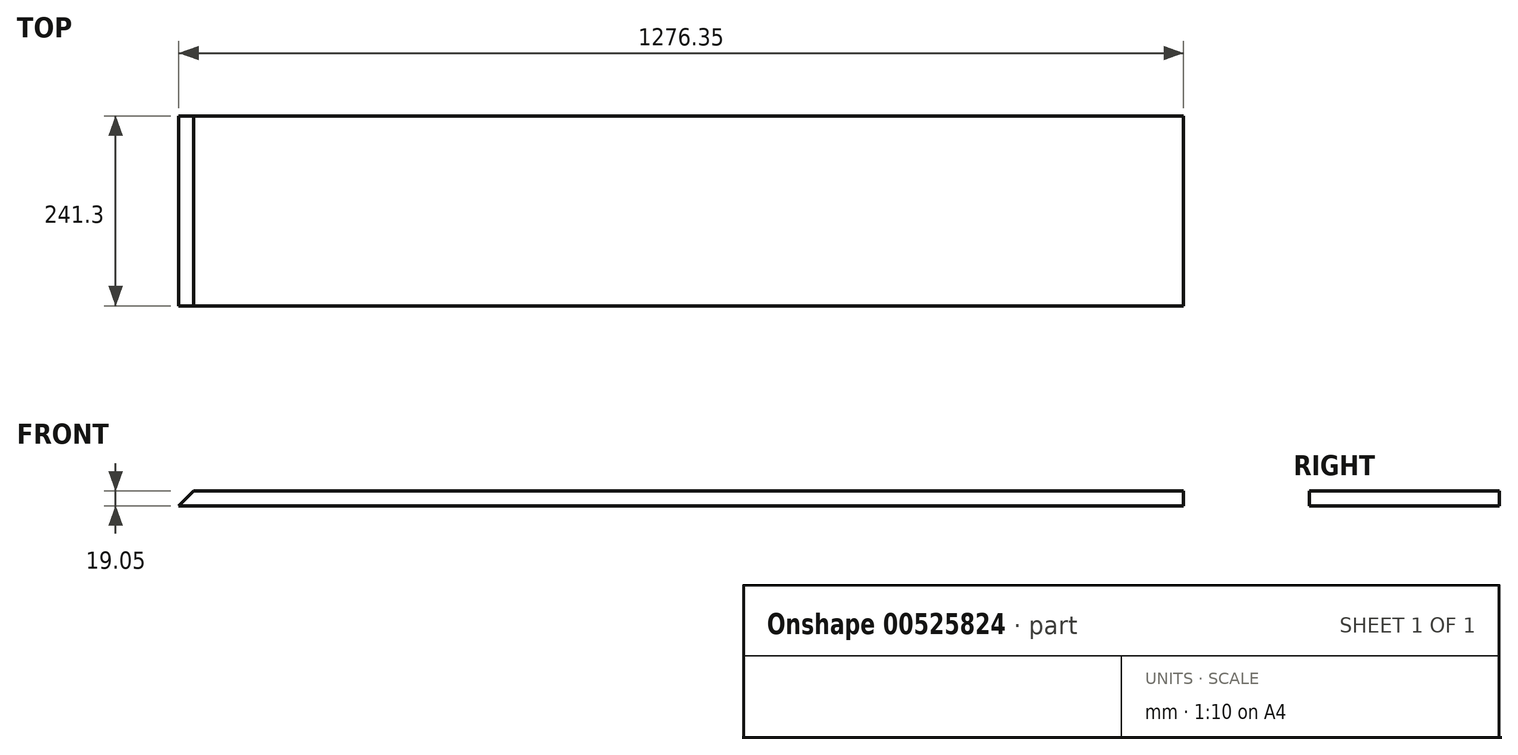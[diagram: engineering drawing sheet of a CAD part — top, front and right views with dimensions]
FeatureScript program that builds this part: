
annotation { "Feature Type Name" : "Feature", "Feature Type Description" : "" }
export const myFeature = defineFeature(function(context is Context, id is Id, definition is map)
    precondition{}
    {
        {
            var Q0;
            Q0=qCreatedBy(makeId("Front.planeOp"),FACE);
            var sketch = newSketch(context, id + "F0", { "sketchPlane" : qUnion([Q0])});
            skLineSegment(sketch, "E0.bottom", {"start": v(-73.76, -19.05) * mm, "end": v(1202.59, -19.05) * mm});
            skLineSegment(sketch, "E0.top", {"start": v(-73.76, 0) * mm, "end": v(1202.59, 0) * mm});
            skLineSegment(sketch, "E0.left", {"start": v(-73.76, -19.05) * mm, "end": v(-73.76, 0) * mm});
            skLineSegment(sketch, "E0.right", {"start": v(1202.59, -19.05) * mm, "end": v(1202.59, 0) * mm});
            skSolve(sketch);
        }
        {
            var Q0;
            Q0=qSketchRegion(id+"F0",true);
            extrude(context, id + "F1", {"entities" : qUnion([Q0]), "depth" : 241.3 * mm});
        }
        {
            var Q0;
            Q0=makeQuery(id+"F1.opExtrude","SWEPT_BODY",BODY,{"disambiguationData":[OSD([sQuery(id+"F0.wireOp",EDGE,"E0.bottom"),sQuery(id+"F0.wireOp",EDGE,"E0.top"),sQuery(id+"F0.wireOp",EDGE,"E0.left"),sQuery(id+"F0.wireOp",EDGE,"E0.right")])]});
            transform(context, id + "F2", {"entities" : qUnion([Q0]), "transformType" : TransformType.TRANSLATION_3D, "dx" : 0 * mm, "dy" : 0 * mm, "dz" : 381 * mm, "makeCopy" : true});
        }
        {
            var Q0;
            Q0=makeQuery(id+"F2.opPattern","COPY",BODY,{"derivedFrom":makeQuery(id+"F1.opExtrude","SWEPT_BODY",BODY,{"disambiguationData":[OSD([sQuery(id+"F0.wireOp",EDGE,"E0.bottom"),sQuery(id+"F0.wireOp",EDGE,"E0.top"),sQuery(id+"F0.wireOp",EDGE,"E0.left"),sQuery(id+"F0.wireOp",EDGE,"E0.right")])]}),"instanceName":"1"});
            deleteBodies(context, id + "F3", {"entities" : qUnion([Q0])});
        }
        {
            var Q0;
            Q0=makeQuery(id+"F1.opExtrude","CAP_FACE",FACE,{"disambiguationData":[OSD([sQuery(id+"F0.wireOp",EDGE,"E0.bottom"),sQuery(id+"F0.wireOp",EDGE,"E0.top"),sQuery(id+"F0.wireOp",EDGE,"E0.left"),sQuery(id+"F0.wireOp",EDGE,"E0.right")])],"isStart":false});
            var sketch = newSketch(context, id + "F4", { "sketchPlane" : qUnion([Q0])});
            skLineSegment(sketch, "E1", {"start": v(-73.76, -19.05) * mm, "end": v(-73.76, 0) * mm});
            skLineSegment(sketch, "E2", {"start": v(-73.76, 0) * mm, "end": v(-54.71, 0) * mm});
            skLineSegment(sketch, "E3", {"start": v(-54.71, 0) * mm, "end": v(-73.76, -19.05) * mm});
            skSolve(sketch);
        }
        {
            var Q0;
            Q0=qSketchRegion(id+"F4",true);
            extrude(context, id + "F5", {"entities" : qUnion([Q0]), "operationType" : NewBodyOperationType.REMOVE, "endBound" : BoundingType.THROUGH_ALL, "oppositeDirection" : true, "depth" : 25.4 * mm});
        }
    });
